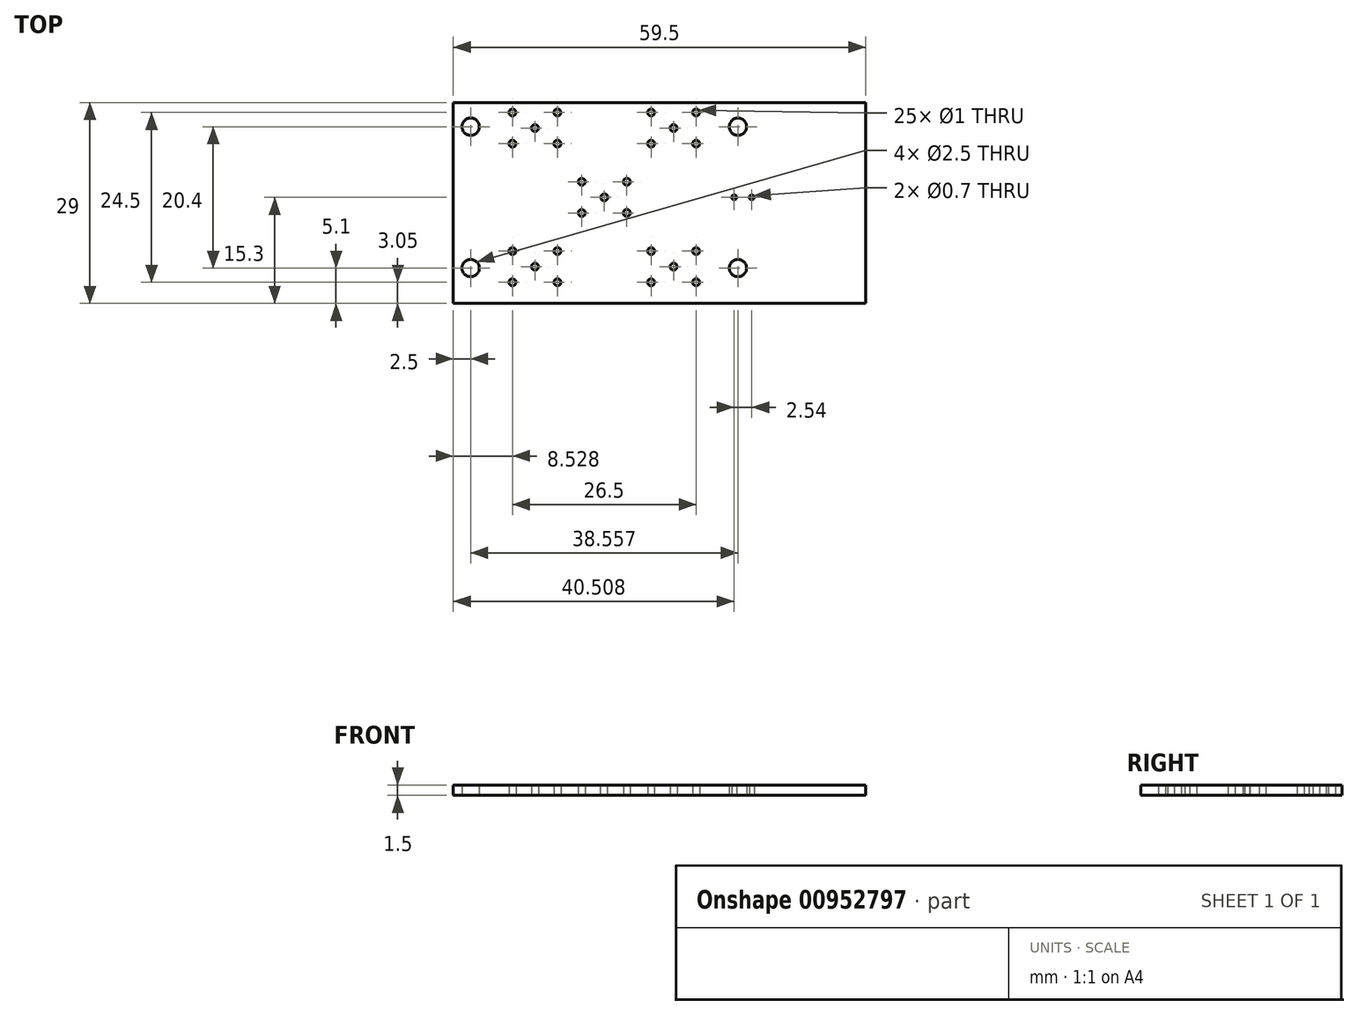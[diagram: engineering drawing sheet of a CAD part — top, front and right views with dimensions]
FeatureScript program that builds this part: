
annotation { "Feature Type Name" : "Feature", "Feature Type Description" : "" }
export const myFeature = defineFeature(function(context is Context, id is Id, definition is map)
    precondition{}
    {
        {
            var Q0;
            Q0=qCreatedBy(makeId("Top.planeOp"),FACE);
            var sketch = newSketch(context, id + "F0", { "sketchPlane" : qUnion([Q0])});
            skLineSegment(sketch, "E0.bottom", {"start": v(0, 0) * mm, "end": v(59.5, 0) * mm});
            skLineSegment(sketch, "E0.top", {"start": v(0, -29) * mm, "end": v(59.5, -29) * mm});
            skLineSegment(sketch, "E0.left", {"start": v(0, 0) * mm, "end": v(0, -29) * mm});
            skLineSegment(sketch, "E0.right", {"start": v(59.5, 0) * mm, "end": v(59.5, -29) * mm});
            skCircle(sketch, "E1", {"center": v(2.5, -3.5) * mm, "radius": 1.25 * mm});
            skCircle(sketch, "E2", {"center": v(41.06, -3.5) * mm, "radius": 1.25 * mm});
            skCircle(sketch, "E3", {"center": v(41.06, -23.9) * mm, "radius": 1.25 * mm});
            skCircle(sketch, "E4", {"center": v(2.5, -23.9) * mm, "radius": 1.25 * mm});
            skPoint(sketch, "E5.middle", {"position": v(21.78, -13.7) * mm});
            skPoint(sketch, "E6.endSnap0", {"position": v(25.03, -13.7) * mm});
            skCircle(sketch, "E7", {"center": v(8.53, -1.45) * mm, "radius": 0.5 * mm});
            skCircle(sketch, "E8", {"center": v(15.03, -1.45) * mm, "radius": 0.5 * mm});
            skCircle(sketch, "E9", {"center": v(15.03, -5.95) * mm, "radius": 0.5 * mm});
            skCircle(sketch, "E10", {"center": v(8.53, -5.95) * mm, "radius": 0.5 * mm});
            skCircle(sketch, "E11", {"center": v(28.53, -1.45) * mm, "radius": 0.5 * mm});
            skCircle(sketch, "E12", {"center": v(35.03, -1.45) * mm, "radius": 0.5 * mm});
            skCircle(sketch, "E13", {"center": v(35.03, -5.95) * mm, "radius": 0.5 * mm});
            skCircle(sketch, "E14", {"center": v(28.53, -5.95) * mm, "radius": 0.5 * mm});
            skCircle(sketch, "E15", {"center": v(18.53, -11.45) * mm, "radius": 0.5 * mm});
            skCircle(sketch, "E16", {"center": v(25.03, -15.95) * mm, "radius": 0.5 * mm});
            skCircle(sketch, "E17", {"center": v(18.53, -15.95) * mm, "radius": 0.5 * mm});
            skCircle(sketch, "E18", {"center": v(25.03, -11.45) * mm, "radius": 0.5 * mm});
            skCircle(sketch, "E19", {"center": v(8.53, -21.45) * mm, "radius": 0.5 * mm});
            skCircle(sketch, "E20", {"center": v(15.03, -21.45) * mm, "radius": 0.5 * mm});
            skCircle(sketch, "E21", {"center": v(8.53, -25.95) * mm, "radius": 0.5 * mm});
            skCircle(sketch, "E22", {"center": v(15.03, -25.95) * mm, "radius": 0.5 * mm});
            skCircle(sketch, "E23", {"center": v(28.53, -21.45) * mm, "radius": 0.5 * mm});
            skCircle(sketch, "E24", {"center": v(35.03, -21.45) * mm, "radius": 0.5 * mm});
            skCircle(sketch, "E25", {"center": v(35.03, -25.95) * mm, "radius": 0.5 * mm});
            skCircle(sketch, "E26", {"center": v(28.53, -25.95) * mm, "radius": 0.5 * mm});
            skCircle(sketch, "E27", {"center": v(40.5, -13.7) * mm, "radius": 0.35 * mm});
            skCircle(sketch, "E28", {"center": v(43.05, -13.7) * mm, "radius": 0.35 * mm});
            skPoint(sketch, "E29.startSnap0", {"position": v(41.78, -13.7) * mm});
            skCircle(sketch, "E30", {"center": v(11.78, -3.7) * mm, "radius": 0.5 * mm});
            skCircle(sketch, "E31", {"center": v(31.78, -3.7) * mm, "radius": 0.5 * mm});
            skCircle(sketch, "E32", {"center": v(31.78, -23.7) * mm, "radius": 0.5 * mm});
            skCircle(sketch, "E33", {"center": v(11.78, -23.7) * mm, "radius": 0.5 * mm});
            skSolve(sketch);
        }
        {
            var Q0;
            Q0=makeQuery(id+"F0.imprint","IMPRINT",FACE,{"disambiguationData":[TD([[makeQuery(id+"F0.imprint","IMPRINT",EDGE,{"derivedFrom":sQuery(id+"F0.wireOp",EDGE,"E0.bottom")}),-1.0]])]});
            extrude(context, id + "F1", {"entities" : qUnion([Q0]), "depth" : 1.5 * mm, "offsetDistance" : 25 * mm});
        }
        {
            var Q0;
            Q0=makeQuery(id+"F1.opExtrude","CAP_FACE",FACE,{"disambiguationData":[OSD([sQuery(id+"F0.wireOp",EDGE,"E0.bottom"),sQuery(id+"F0.wireOp",EDGE,"E0.top"),sQuery(id+"F0.wireOp",EDGE,"E0.left"),sQuery(id+"F0.wireOp",EDGE,"E0.right"),sQuery(id+"F0.wireOp",EDGE,"E1"),sQuery(id+"F0.wireOp",EDGE,"E2"),sQuery(id+"F0.wireOp",EDGE,"E3"),sQuery(id+"F0.wireOp",EDGE,"E4"),sQuery(id+"F0.wireOp",EDGE,"E7"),sQuery(id+"F0.wireOp",EDGE,"E8"),sQuery(id+"F0.wireOp",EDGE,"E9"),sQuery(id+"F0.wireOp",EDGE,"E10"),sQuery(id+"F0.wireOp",EDGE,"E11"),sQuery(id+"F0.wireOp",EDGE,"E12"),sQuery(id+"F0.wireOp",EDGE,"E13"),sQuery(id+"F0.wireOp",EDGE,"E14"),sQuery(id+"F0.wireOp",EDGE,"E15"),sQuery(id+"F0.wireOp",EDGE,"E16"),sQuery(id+"F0.wireOp",EDGE,"E17"),sQuery(id+"F0.wireOp",EDGE,"E18"),sQuery(id+"F0.wireOp",EDGE,"E19"),sQuery(id+"F0.wireOp",EDGE,"E20"),sQuery(id+"F0.wireOp",EDGE,"E21"),sQuery(id+"F0.wireOp",EDGE,"E22"),sQuery(id+"F0.wireOp",EDGE,"E23"),sQuery(id+"F0.wireOp",EDGE,"E24"),sQuery(id+"F0.wireOp",EDGE,"E25"),sQuery(id+"F0.wireOp",EDGE,"E26"),sQuery(id+"F0.wireOp",EDGE,"E27"),sQuery(id+"F0.wireOp",EDGE,"E28")])],"isStart":false});
            var sketch = newSketch(context, id + "F2", { "sketchPlane" : qUnion([Q0])});
            skCircle(sketch, "E34", {"center": v(21.78, -13.7) * mm, "radius": 0.5 * mm});
            skSolve(sketch);
        }
        {
            var Q0;
            Q0=makeQuery(id+"F2.imprint","IMPRINT",FACE,{"disambiguationData":[TD([[makeQuery(id+"F2.imprint","IMPRINT",EDGE,{"derivedFrom":sQuery(id+"F2.wireOp",EDGE,"E34")}),1.0]])]});
            extrude(context, id + "F3", {"entities" : qUnion([Q0]), "operationType" : NewBodyOperationType.REMOVE, "oppositeDirection" : true, "depth" : 2 * mm, "offsetDistance" : 25 * mm});
        }
    });
